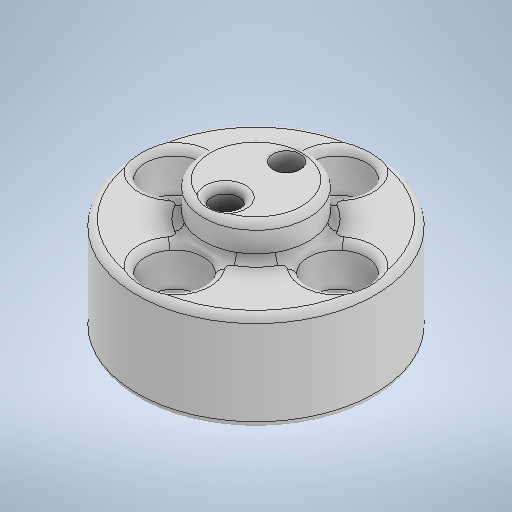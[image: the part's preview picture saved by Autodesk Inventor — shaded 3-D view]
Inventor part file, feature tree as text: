
AUTODESK INVENTOR PART (.ipt)
format: ipt  version: 2025.1 (Build 291241000, 241)  size: 495,104 bytes
history: native  units: mm
features: sketch x5, extrude x4, other x3, hole x1, fillet x1
ambient origin geometry x8: Origin, YZ Plane, XZ Plane, XY Plane, X Axis, Y Axis, Z Axis, Center Point
bodies: Solide1 (feature_tree)
feature tree (14):
  extrude  "Extrusion1"  Depth=35.0mm
  extrude  "Extrusion2"  Depth=24.0mm
  extrude  "Extrusion4"  Depth=4.0mm
  extrude  "Extrusion3"  Depth=14.5mm TaperAngle=0.0deg
  hole  "Perçage1"  [1 undecoded]
  fillet  "Congé2"  Radius=8.5mm
  sketch  "Esquisse1"
  sketch  "Esquisse2"
  other  "Réseau d'esquisse circulaire2"
  other  "Réseau d'esquisse circulaire3"
  sketch  "Esquisse3"
  sketch  "Esquisse5"
  sketch  "Esquisse6"
  other  "Réseau d'esquisse circulaire5"
note: 1 required parameter value undecoded (feature->parameter linkage not recoverable at this tier; creation-order binding heuristic only, values carry confidence <= 0.55)
